# Revit family: CC_SEñales
name_source: partatom
category: Parking
revit_build: Autodesk Revit 2018 (Build: 20190510_1515(x64)
units: mm (PartAtom-declared; Revit-internal decimal feet)

## family parameters
Always vertical = Yes
Cut with Voids When Loaded = No
Shared = No
Work Plane-Based = No

## types (6) — shared parameters
CC.Palo.Ancho = 100 mm  [stored 0.328084 ft]
CC.Palo.Profundidad = 50 mm  [stored 0.164042 ft]
Panel.Espesor = 40 mm
Panel.Prohibido.Diametro = 900 mm  [stored 2.95276 ft]
Panel.Prohibido.Diametro.Interior = 780 mm  [stored 2.55906 ft]
tipo grafico = CC_Panel_GraficoCruIzq
tipo1 = CC_Panel_GraficoCurvIzq

## per-type parameters (varying)
| type | Grafico.Cruce.Izq | Grafico.Curva.Der | Grafico.Curva.Izq | Panel.Fondo |
| Panel.Definitivo.CurvaIzq | No | Yes | No | Panel.Blanco |
| Panel.Definitivo.CurvaDer | No | Yes | No | Panel.Blanco |
| Panel.Obra.CurvaDer | No | Yes | No | Panel.Amarillo |
| Panel.Obra.CurvaIzq | No | No | Yes | Panel.Amarillo |
| Panel.Definitivo.CruceIzq | Yes | No | No | Panel.Amarillo |
| Panel.Obra.CruceIzq | Yes | No | No | Panel.Amarillo |

note: [stored X ft] marks values corroborated as IEEE doubles in the binary element streams (Revit-internal decimal feet)

## geometry (parser evidence)
native form markers: Sweep x16
no freeform markers — native parametric forms only
